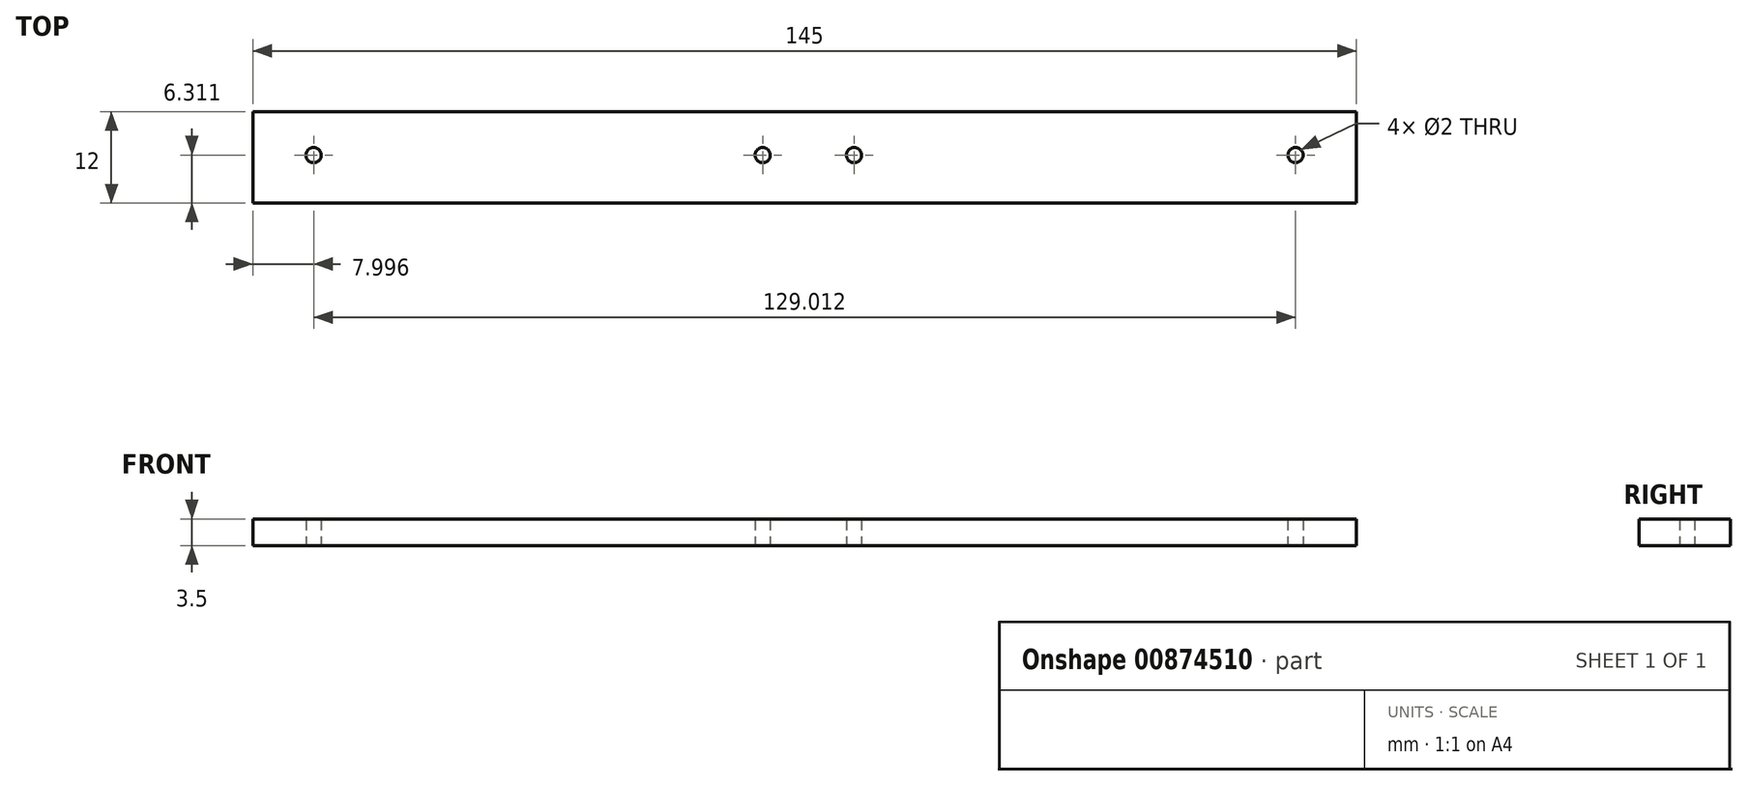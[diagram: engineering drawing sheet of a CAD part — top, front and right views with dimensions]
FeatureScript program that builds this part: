
annotation { "Feature Type Name" : "Feature", "Feature Type Description" : "" }
export const myFeature = defineFeature(function(context is Context, id is Id, definition is map)
    precondition{}
    {
        {
            var Q0;
            Q0=qCreatedBy(makeId("Top.planeOp"),FACE);
            var sketch = newSketch(context, id + "F0", { "sketchPlane" : qUnion([Q0])});
            skLineSegment(sketch, "E0", {"start": v(-69.1, 27.57) * mm, "end": v(75.9, 27.57) * mm});
            skLineSegment(sketch, "E1.left", {"start": v(-69.1, 27.57) * mm, "end": v(-69.1, 15.57) * mm});
            skLineSegment(sketch, "E1.right", {"start": v(75.9, 27.57) * mm, "end": v(75.9, 15.57) * mm});
            skPoint(sketch, "E2", {"position": v(-69.1, 15.57) * mm});
            skPoint(sketch, "E3", {"position": v(75.9, 15.57) * mm});
            skPoint(sketch, "E4", {"position": v(75.9, 27.57) * mm});
            skPoint(sketch, "E5", {"position": v(-69.1, 27.57) * mm});
            skLineSegment(sketch, "E6", {"start": v(-69.1, 15.57) * mm, "end": v(75.9, 15.57) * mm});
            skPoint(sketch, "E7", {"position": v(-54.1, 15.57) * mm});
            skPoint(sketch, "E8", {"position": v(60.9, 15.57) * mm});
            skPoint(sketch, "E9", {"position": v(-46.1, 15.57) * mm});
            skPoint(sketch, "E10", {"position": v(52.9, 15.57) * mm});
            skPoint(sketch, "E11", {"position": v(-23.1, 15.57) * mm});
            skPoint(sketch, "E12", {"position": v(29.9, 15.57) * mm});
            skPoint(sketch, "E13", {"position": v(-15.1, 15.57) * mm});
            skPoint(sketch, "E14", {"position": v(21.9, 15.57) * mm});
            skLineSegment(sketch, "E15.bottom", {"start": v(-46.1, 15.57) * mm, "end": v(-54.1, 15.57) * mm});
            skLineSegment(sketch, "E16.bottom", {"start": v(-15.1, 15.57) * mm, "end": v(-23.2, 15.57) * mm});
            skLineSegment(sketch, "E17.bottom", {"start": v(29.9, 15.57) * mm, "end": v(21.9, 15.57) * mm});
            skLineSegment(sketch, "E18.bottom", {"start": v(60.9, 15.57) * mm, "end": v(52.88, 15.57) * mm});
            skPoint(sketch, "E19", {"position": v(-66.1, 21.88) * mm});
            skPoint(sketch, "E20", {"position": v(-56.1, 21.88) * mm});
            skPoint(sketch, "E21", {"position": v(72.9, 21.53) * mm});
            skPoint(sketch, "E22", {"position": v(62.9, 21.53) * mm});
            skLineSegment(sketch, "E23", {"start": v(-69.1, 21.88) * mm, "end": v(-39.02, 21.88) * mm});
            skPoint(sketch, "E24", {"position": v(-39.1, 21.88) * mm});
            skPoint(sketch, "E25", {"position": v(-29.1, 21.88) * mm});
            skPoint(sketch, "E26", {"position": v(-19.1, 21.88) * mm});
            skPoint(sketch, "E27", {"position": v(-2.1, 21.88) * mm});
            skPoint(sketch, "E28", {"position": v(9.9, 21.88) * mm});
            skPoint(sketch, "E29", {"position": v(25.9, 21.88) * mm});
            skPoint(sketch, "E30", {"position": v(35.9, 21.88) * mm});
            skPoint(sketch, "E31", {"position": v(45.9, 21.88) * mm});
            skLineSegment(sketch, "E32", {"start": v(-39.02, 27.57) * mm, "end": v(-39.02, 15.57) * mm});
            skLineSegment(sketch, "E33", {"start": v(-1.88, 27.57) * mm, "end": v(-1.88, 15.57) * mm});
            skLineSegment(sketch, "E34", {"start": v(9.84, 27.57) * mm, "end": v(9.9, 15.57) * mm});
            skLineSegment(sketch, "E35", {"start": v(59.93, 27.57) * mm, "end": v(59.93, 15.57) * mm});
            skLineSegment(sketch, "E36", {"start": v(72.64, 27.57) * mm, "end": v(72.9, 15.57) * mm});
            skPoint(sketch, "E37", {"position": v(-50.34, 15.57) * mm});
            skPoint(sketch, "E38", {"position": v(-19.14, 15.57) * mm});
            skPoint(sketch, "E39", {"position": v(25.9, 15.57) * mm});
            skPoint(sketch, "E40", {"position": v(-50.05, 27.57) * mm});
            skPoint(sketch, "E41", {"position": v(-19.54, 27.57) * mm});
            skPoint(sketch, "E42", {"position": v(26.37, 27.57) * mm});
            skPoint(sketch, "E43", {"position": v(56.88, 27.57) * mm});
            skPoint(sketch, "E15.top.end.orphan", {"position": v(-54.1, -22.43) * mm});
            skPoint(sketch, "E15.top.start.orphan", {"position": v(-46.1, -22.43) * mm});
            skLineSegment(sketch, "E44.trimOffspring", {"start": v(-19.1, 21.88) * mm, "end": v(25.9, 21.88) * mm});
            skLineSegment(sketch, "E45.trimOffspring", {"start": v(59.93, 21.88) * mm, "end": v(75.9, 21.88) * mm});
            skPoint(sketch, "E46", {"position": v(-61.1, 21.88) * mm});
            skPoint(sketch, "E47", {"position": v(67.92, 21.88) * mm});
            skPoint(sketch, "E48.end.orphan", {"position": v(-55.88, 15.57) * mm});
            skSolve(sketch);
        }
        {
            var Q0;
            Q0=qSketchRegion(id+"F0",true);
            extrude(context, id + "F1", {"entities" : qUnion([Q0]), "depth" : 3.5 * mm, "offsetDistance" : 25 * mm});
        }
        {
            var Q0;
            Q0=sQuery(id+"F0.wireOp",VERTEX,"E46");
            var Q1;
            Q1=sQuery(id+"F0.wireOp",VERTEX,"E47");
            var Q2;
            Q2=sQuery(id+"F0.wireOp",VERTEX,"E27");
            var Q3;
            Q3=sQuery(id+"F0.wireOp",VERTEX,"E28");
            var Q4;
            Q4=makeQuery(id+"F1.opExtrude","SWEPT_BODY",BODY,{"disambiguationData":[OSD([sQuery(id+"F0.wireOp",EDGE,"E0"),sQuery(id+"F0.wireOp",EDGE,"E1.left"),sQuery(id+"F0.wireOp",EDGE,"E1.right"),sQuery(id+"F0.wireOp",EDGE,"E6"),sQuery(id+"F0.wireOp",EDGE,"E15.bottom"),sQuery(id+"F0.wireOp",EDGE,"E16.bottom"),sQuery(id+"F0.wireOp",EDGE,"E17.bottom"),sQuery(id+"F0.wireOp",EDGE,"E18.bottom")])]});
            hole(context, id + "F2", {"style" : HoleStyle.SIMPLE, "endStyle" : HoleEndStyle.THROUGH, "oppositeDirection" : true, "holeDiameter" : 2 * mm, "majorDiameter" : 5 * mm, "isTappedThrough" : true, "tappedDepth" : 12 * mm, "tapClearance" : 3, "locations" : qUnion([Q0, Q1, Q2, Q3]), "scope" : qUnion([Q4])});
        }
    });
